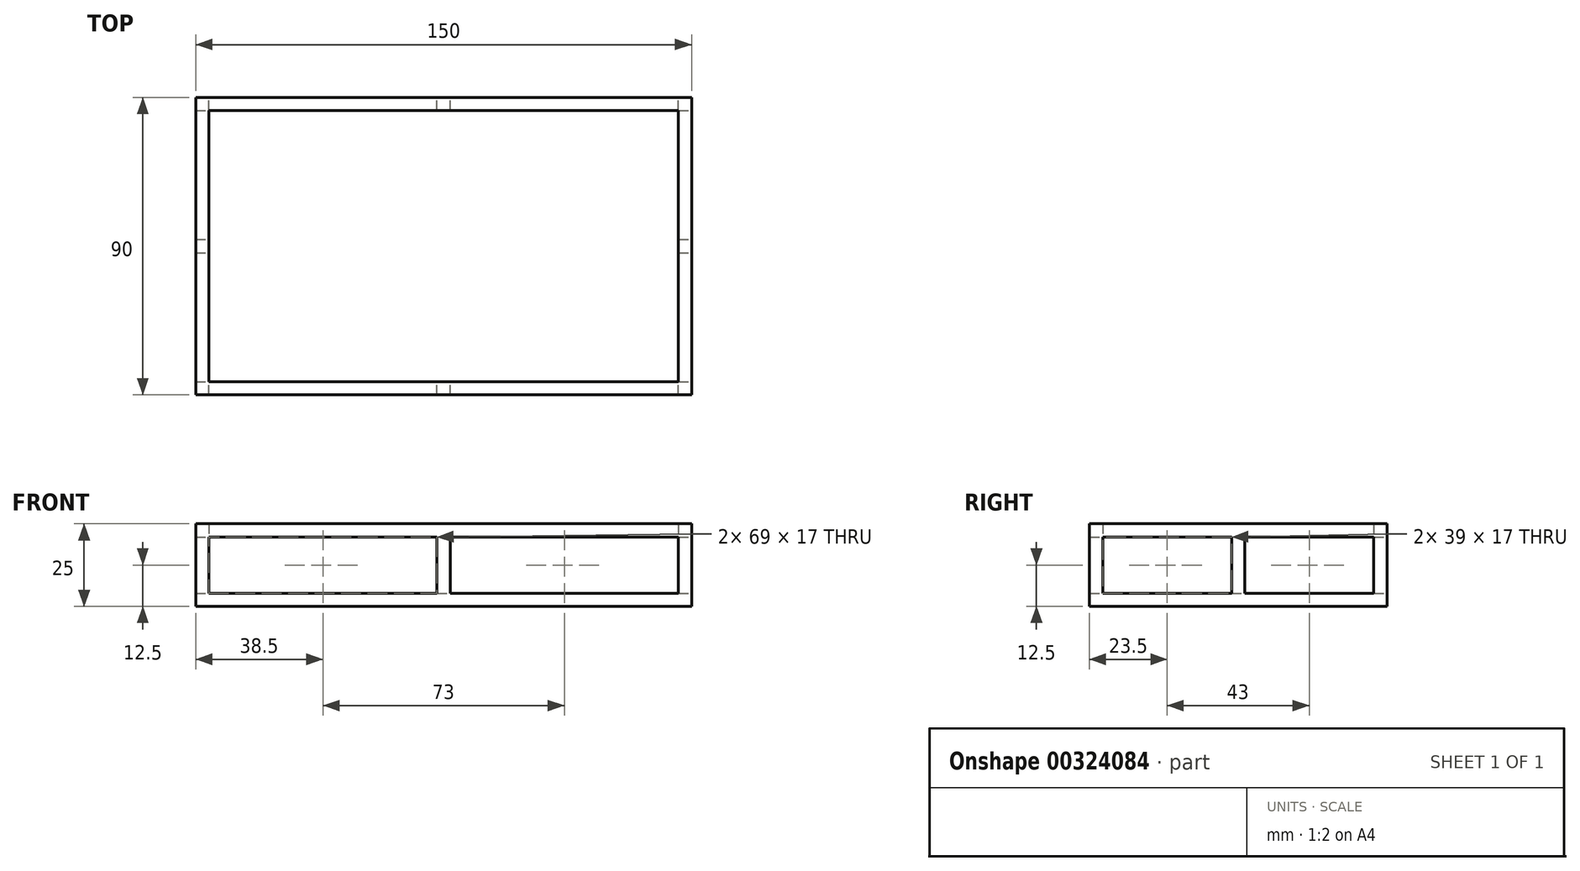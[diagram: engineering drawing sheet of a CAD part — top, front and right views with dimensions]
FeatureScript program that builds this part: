
annotation { "Feature Type Name" : "Feature", "Feature Type Description" : "" }
export const myFeature = defineFeature(function(context is Context, id is Id, definition is map)
    precondition{}
    {
        {
            var Q0;
            Q0=qCreatedBy(makeId("Front.planeOp"),FACE);
            var sketch = newSketch(context, id + "F0", { "sketchPlane" : qUnion([Q0])});
            skLineSegment(sketch, "E0.bottom", {"start": v(0, 0) * mm, "end": v(-75, 0) * mm});
            skLineSegment(sketch, "E0.top", {"start": v(0, 25) * mm, "end": v(-75, 25) * mm});
            skLineSegment(sketch, "E0.left", {"start": v(0, 0) * mm, "end": v(0, 25) * mm});
            skLineSegment(sketch, "E0.right", {"start": v(-75, 0) * mm, "end": v(-75, 25) * mm});
            skLineSegment(sketch, "E1.MirrorCS", {"start": v(0, 25) * mm, "end": v(75, 25) * mm});
            skLineSegment(sketch, "E2.MirrorCS", {"start": v(75, 0) * mm, "end": v(75, 25) * mm});
            skLineSegment(sketch, "E3.MirrorCS", {"start": v(0, 0) * mm, "end": v(75, 0) * mm});
            skLineSegment(sketch, "E4.bottom", {"start": v(-2, 4) * mm, "end": v(-71, 4) * mm});
            skLineSegment(sketch, "E4.top", {"start": v(-2, 21) * mm, "end": v(-71, 21) * mm});
            skLineSegment(sketch, "E4.left", {"start": v(-2, 4) * mm, "end": v(-2, 21) * mm});
            skLineSegment(sketch, "E4.right", {"start": v(-71, 4) * mm, "end": v(-71, 21) * mm});
            skLineSegment(sketch, "E5.MirrorCS", {"start": v(2, 21) * mm, "end": v(71, 21) * mm});
            skLineSegment(sketch, "E6.MirrorCS", {"start": v(71, 4) * mm, "end": v(71, 21) * mm});
            skLineSegment(sketch, "E7.MirrorCS", {"start": v(2, 4) * mm, "end": v(71, 4) * mm});
            skLineSegment(sketch, "E8.MirrorCS", {"start": v(2, 4) * mm, "end": v(2, 21) * mm});
            skSolve(sketch);
        }
        {
            var Q0;
            Q0=makeQuery(id+"F0.imprint","IMPRINT",FACE,{"disambiguationData":[TD([[makeQuery(id+"F0.imprint","IMPRINT",EDGE,{"derivedFrom":sQuery(id+"F0.wireOp",EDGE,"E0.bottom")}),-1.0]])]});
            var Q1;
            Q1=makeQuery(id+"F0.imprint","IMPRINT",FACE,{"disambiguationData":[TD([[makeQuery(id+"F0.imprint","IMPRINT",EDGE,{"derivedFrom":sQuery(id+"F0.wireOp",EDGE,"E0.left")}),-1.0]])]});
            extrude(context, id + "F1", {"entities" : qUnion([Q0, Q1]), "endBound" : BoundingType.SYMMETRIC, "depth" : 90 * mm});
        }
        {
            var Q0;
            Q0=qCreatedBy(makeId("Right.planeOp"),FACE);
            var sketch = newSketch(context, id + "F2", { "sketchPlane" : qUnion([Q0])});
            skLineSegment(sketch, "E9.bottom", {"start": v(-2, 4) * mm, "end": v(-41, 4) * mm});
            skLineSegment(sketch, "E9.top", {"start": v(-2, 21) * mm, "end": v(-41, 21) * mm});
            skLineSegment(sketch, "E9.left", {"start": v(-2, 4) * mm, "end": v(-2, 21) * mm});
            skLineSegment(sketch, "E9.right", {"start": v(-41, 4) * mm, "end": v(-41, 21) * mm});
            skLineSegment(sketch, "E10", {"start": v(0, 0) * mm, "end": v(0, 33.78) * mm, "construction": true});
            skLineSegment(sketch, "E11.MirrorCS", {"start": v(2, 21) * mm, "end": v(41, 21) * mm});
            skLineSegment(sketch, "E12.MirrorCS", {"start": v(2, 4) * mm, "end": v(2, 21) * mm});
            skLineSegment(sketch, "E13.MirrorCS", {"start": v(2, 4) * mm, "end": v(41, 4) * mm});
            skLineSegment(sketch, "E14.MirrorCS", {"start": v(41, 4) * mm, "end": v(41, 21) * mm});
            skSolve(sketch);
        }
        {
            var Q0;
            Q0=makeQuery(id+"F2.imprint","IMPRINT",FACE,{"disambiguationData":[TD([[makeQuery(id+"F2.imprint","IMPRINT",EDGE,{"derivedFrom":sQuery(id+"F2.wireOp",EDGE,"E11.MirrorCS")}),-1.0]])]});
            var Q1;
            Q1=makeQuery(id+"F2.imprint","IMPRINT",FACE,{"disambiguationData":[TD([[makeQuery(id+"F2.imprint","IMPRINT",EDGE,{"derivedFrom":sQuery(id+"F2.wireOp",EDGE,"E9.bottom")}),-1.0]])]});
            extrude(context, id + "F3", {"entities" : qUnion([Q0, Q1]), "operationType" : NewBodyOperationType.REMOVE, "endBound" : BoundingType.SYMMETRIC, "oppositeDirection" : true, "depth" : 200 * mm});
        }
        {
            var Q0;
            Q0=qCreatedBy(makeId("Top.planeOp"),FACE);
            var sketch = newSketch(context, id + "F4", { "sketchPlane" : qUnion([Q0])});
            skLineSegment(sketch, "E15.bottom", {"start": v(-71, 41) * mm, "end": v(71, 41) * mm});
            skLineSegment(sketch, "E15.top", {"start": v(-71, -41) * mm, "end": v(71, -41) * mm});
            skLineSegment(sketch, "E15.left", {"start": v(-71, 41) * mm, "end": v(-71, -41) * mm});
            skLineSegment(sketch, "E15.right", {"start": v(71, 41) * mm, "end": v(71, -41) * mm});
            skPoint(sketch, "E15.middle", {"position": v(0, 0) * mm});
            skSolve(sketch);
        }
        {
            var Q0;
            Q0 = qSketchRegion(id + "F4", true);
            extrude(context, id + "F5", {"entities" : qUnion([Q0]), "operationType" : NewBodyOperationType.REMOVE, "depth" : 30 * mm, "hasSecondDirection" : true, "secondDirectionOppositeDirection" : false, "secondDirectionDepth" : 4 * mm});
        }
    });
